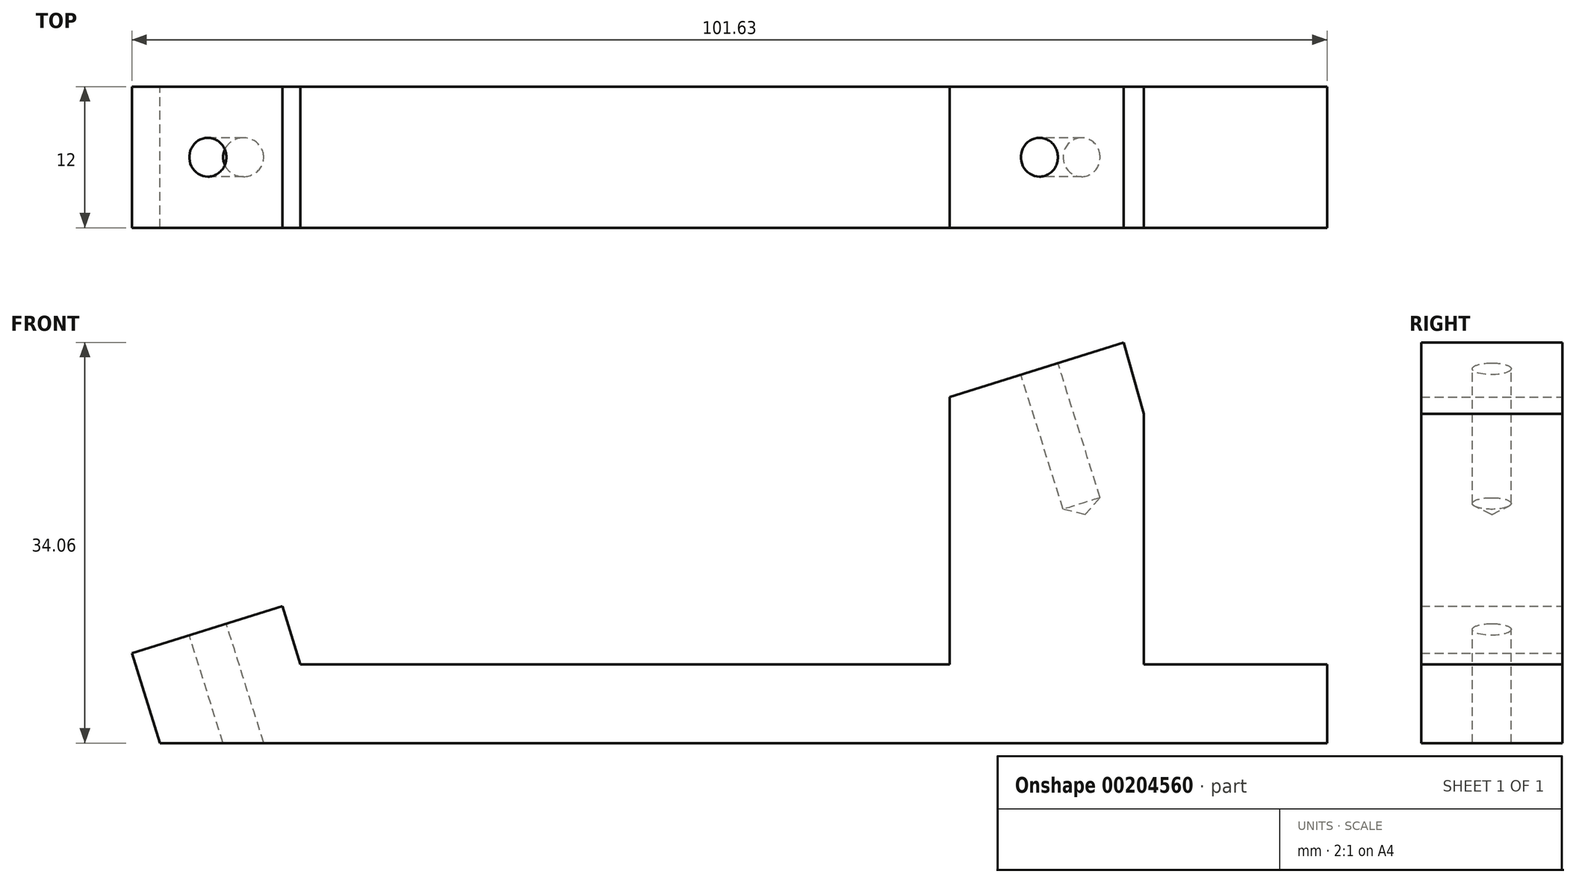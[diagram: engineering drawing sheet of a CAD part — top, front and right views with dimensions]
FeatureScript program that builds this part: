
annotation { "Feature Type Name" : "Feature", "Feature Type Description" : "" }
export const myFeature = defineFeature(function(context is Context, id is Id, definition is map)
    precondition{}
    {
        {
            var Q0;
            Q0=qCreatedBy(makeId("Front.planeOp"),FACE);
            var sketch = newSketch(context, id + "F0", { "sketchPlane" : qUnion([Q0])});
            skLineSegment(sketch, "E0.bottom", {"start": v(14.34, 6.7) * mm, "end": v(69.53, 6.7) * mm});
            skLineSegment(sketch, "E0.top", {"start": v(2.4, 0) * mm, "end": v(101.63, 0) * mm});
            skLineSegment(sketch, "E0.right", {"start": v(101.63, 6.7) * mm, "end": v(101.63, 0) * mm});
            skLineSegment(sketch, "E1.left", {"start": v(86.03, 6.7) * mm, "end": v(86.03, 28) * mm});
            skLineSegment(sketch, "E2.trimOffspring", {"start": v(86.03, 6.7) * mm, "end": v(101.63, 6.7) * mm});
            skLineSegment(sketch, "E3", {"start": v(69.53, 6.7) * mm, "end": v(69.53, 29.43) * mm});
            skLineSegment(sketch, "E4", {"start": v(86.03, 28) * mm, "end": v(84.33, 34.06) * mm});
            skLineSegment(sketch, "E5", {"start": v(2.4, 0) * mm, "end": v(0, 7.63) * mm});
            skLineSegment(sketch, "E6", {"start": v(12.79, 11.64) * mm, "end": v(14.34, 6.7) * mm});
            skLineSegment(sketch, "E7", {"start": v(0, 7.63) * mm, "end": v(12.79, 11.64) * mm});
            skLineSegment(sketch, "E8.trimOffspring", {"start": v(69.53, 29.43) * mm, "end": v(84.33, 34.06) * mm});
            skPoint(sketch, "E9", {"position": v(6.4, 9.64) * mm});
            skPoint(sketch, "E10", {"position": v(77.17, 31.82) * mm});
            skSolve(sketch);
        }
        {
            var Q0;
            Q0 = qSketchRegion(id + "F0", true);
            extrude(context, id + "F1", {"entities" : qUnion([Q0]), "endBound" : BoundingType.SYMMETRIC, "depth" : 12 * mm});
        }
        {
            var Q0;
            Q0=makeQuery(id+"F1.opExtrude","SWEPT_FACE",FACE,{"disambiguationData":[OSD([sQuery(id+"F0.wireOp",EDGE,"E7")])]});
            var sketch = newSketch(context, id + "F2", { "sketchPlane" : qUnion([Q0])});
            skCircle(sketch, "E11", {"center": v(9.05, 0) * mm, "radius": 2 * mm});
            skSolve(sketch);
        }
        {
            var Q0;
            Q0=sQuery(id+"F2.wireOp",VERTEX,"E11.center");
            var Q1;
            Q1=makeQuery(id+"F1.opExtrude","SWEPT_BODY",BODY,{"disambiguationData":[OSD([sQuery(id+"F0.wireOp",EDGE,"E0.bottom"),sQuery(id+"F0.wireOp",EDGE,"E0.top"),sQuery(id+"F0.wireOp",EDGE,"E0.right"),sQuery(id+"F0.wireOp",EDGE,"E1.left"),sQuery(id+"F0.wireOp",EDGE,"E2.trimOffspring"),sQuery(id+"F0.wireOp",EDGE,"E3"),sQuery(id+"F0.wireOp",EDGE,"E4"),sQuery(id+"F0.wireOp",EDGE,"E5"),sQuery(id+"F0.wireOp",EDGE,"E6"),sQuery(id+"F0.wireOp",EDGE,"E7"),sQuery(id+"F0.wireOp",EDGE,"E8.trimOffspring")])]});
            hole(context, id + "F3", {"style" : HoleStyle.SIMPLE, "endStyle" : HoleEndStyle.BLIND, "standardTappedOrClearance" : lookupTablePath({ "standard" : "ISO", "engagement" : "75%", "pitch" : "0.7 mm", "size" : "M4", "type" : "Tapped" }), "standardBlindInLast" : lookupTablePath({ "standard" : "ISO", "engagement" : "75%", "pitch" : "0.7 mm", "size" : "M4", "type" : "Tapped" }), "holeDiameter" : 3.3 * mm, "holeDepth" : 12 * mm, "locations" : qUnion([Q0]), "scope" : qUnion([Q1]), "majorDiameter" : 4 * mm});
        }
        {
            var Q0;
            Q0=makeQuery(id+"F1.opExtrude","SWEPT_FACE",FACE,{"disambiguationData":[OSD([sQuery(id+"F0.wireOp",EDGE,"E8.trimOffspring")])]});
            var sketch = newSketch(context, id + "F4", { "sketchPlane" : qUnion([Q0])});
            skPoint(sketch, "E12", {"position": v(83.15, 0) * mm});
            skSolve(sketch);
        }
        {
            var Q0;
            Q0=sQuery(id+"F4.wireOp",VERTEX,"E12");
            var Q1;
            Q1=makeQuery(id+"F1.opExtrude","SWEPT_BODY",BODY,{"disambiguationData":[OSD([sQuery(id+"F0.wireOp",EDGE,"E0.bottom"),sQuery(id+"F0.wireOp",EDGE,"E0.top"),sQuery(id+"F0.wireOp",EDGE,"E0.right"),sQuery(id+"F0.wireOp",EDGE,"E1.left"),sQuery(id+"F0.wireOp",EDGE,"E2.trimOffspring"),sQuery(id+"F0.wireOp",EDGE,"E3"),sQuery(id+"F0.wireOp",EDGE,"E4"),sQuery(id+"F0.wireOp",EDGE,"E5"),sQuery(id+"F0.wireOp",EDGE,"E6"),sQuery(id+"F0.wireOp",EDGE,"E7"),sQuery(id+"F0.wireOp",EDGE,"E8.trimOffspring")])]});
            hole(context, id + "F5", {"style" : HoleStyle.SIMPLE, "endStyle" : HoleEndStyle.BLIND, "standardTappedOrClearance" : lookupTablePath({ "standard" : "ISO", "engagement" : "75%", "pitch" : "0.7 mm", "size" : "M4", "type" : "Tapped" }), "standardBlindInLast" : lookupTablePath({ "standard" : "ISO", "engagement" : "75%", "pitch" : "0.7 mm", "size" : "M4", "type" : "Tapped" }), "holeDiameter" : 3.3 * mm, "holeDepth" : 12 * mm, "locations" : qUnion([Q0]), "scope" : qUnion([Q1]), "majorDiameter" : 4 * mm});
        }
    });
